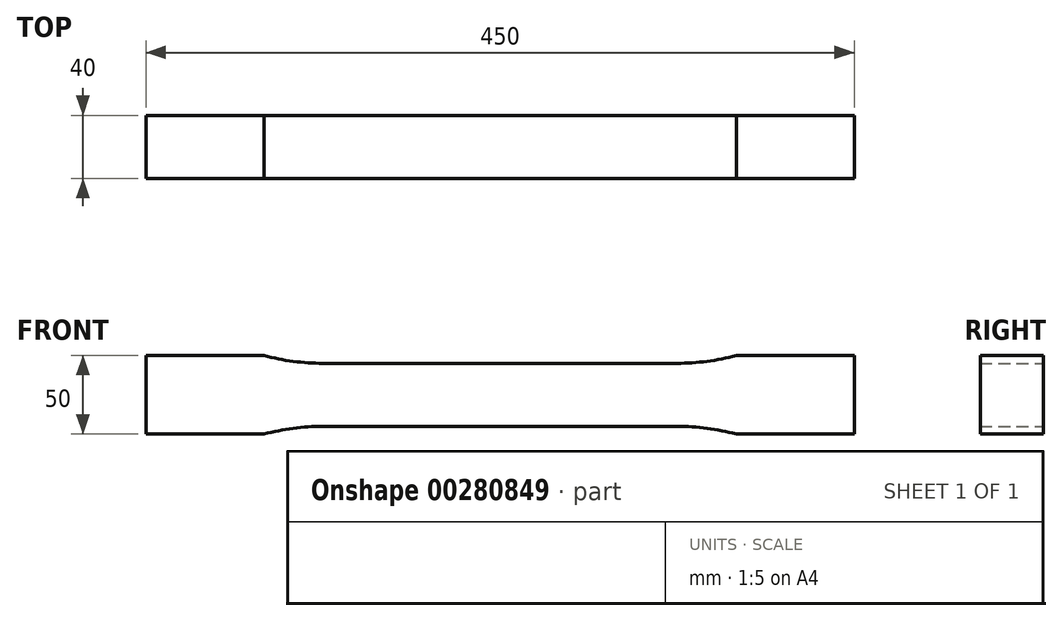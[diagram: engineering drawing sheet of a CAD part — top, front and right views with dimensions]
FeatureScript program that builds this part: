
annotation { "Feature Type Name" : "Feature", "Feature Type Description" : "" }
export const myFeature = defineFeature(function(context is Context, id is Id, definition is map)
    precondition{}
    {
        {
            var Q0;
            Q0=qCreatedBy(makeId("Front.planeOp"),FACE);
            var sketch = newSketch(context, id + "F0", { "sketchPlane" : qUnion([Q0])});
            skLineSegment(sketch, "E0", {"start": v(0, 20) * mm, "end": v(112.5, 20) * mm});
            skLineSegment(sketch, "E1", {"start": v(150, 25) * mm, "end": v(225, 25) * mm});
            skLineSegment(sketch, "E2.MirrorCS", {"start": v(0, -20) * mm, "end": v(112.5, -20) * mm});
            skLineSegment(sketch, "E3.MirrorCS", {"start": v(150, -25) * mm, "end": v(225, -25) * mm});
            skLineSegment(sketch, "E4.MirrorCS", {"start": v(-150, -25) * mm, "end": v(-225, -25) * mm});
            skLineSegment(sketch, "E5.MirrorCS", {"start": v(-150, 25) * mm, "end": v(-225, 25) * mm});
            skLineSegment(sketch, "E6.MirrorCS", {"start": v(0, -20) * mm, "end": v(-112.5, -20) * mm});
            skLineSegment(sketch, "E7.MirrorCS", {"start": v(0, 20) * mm, "end": v(-112.5, 20) * mm});
            skLineSegment(sketch, "E8", {"start": v(-225, 25) * mm, "end": v(-225, -25) * mm});
            skLineSegment(sketch, "E9", {"start": v(225, 25) * mm, "end": v(225, -25) * mm});
            skArc(sketch, "E10", {"start": v(-150, 25) * mm, "mid": v(-131.42, 21.26) * mm, "end": v(-112.5, 20) * mm});
            skArc(sketch, "E11", {"start": v(112.5, 20) * mm, "mid": v(131.42, 21.26) * mm, "end": v(150, 25) * mm});
            skArc(sketch, "E12", {"start": v(150, -25) * mm, "mid": v(131.42, -21.26) * mm, "end": v(112.5, -20) * mm});
            skArc(sketch, "E13", {"start": v(-112.5, -20) * mm, "mid": v(-131.42, -21.26) * mm, "end": v(-150, -25) * mm});
            skSolve(sketch);
        }
        {
            var Q0;
            Q0 = qSketchRegion(id + "F0", true);
            extrude(context, id + "F1", {"entities" : qUnion([Q0]), "endBound" : BoundingType.SYMMETRIC, "depth" : 40 * mm});
        }
    });
